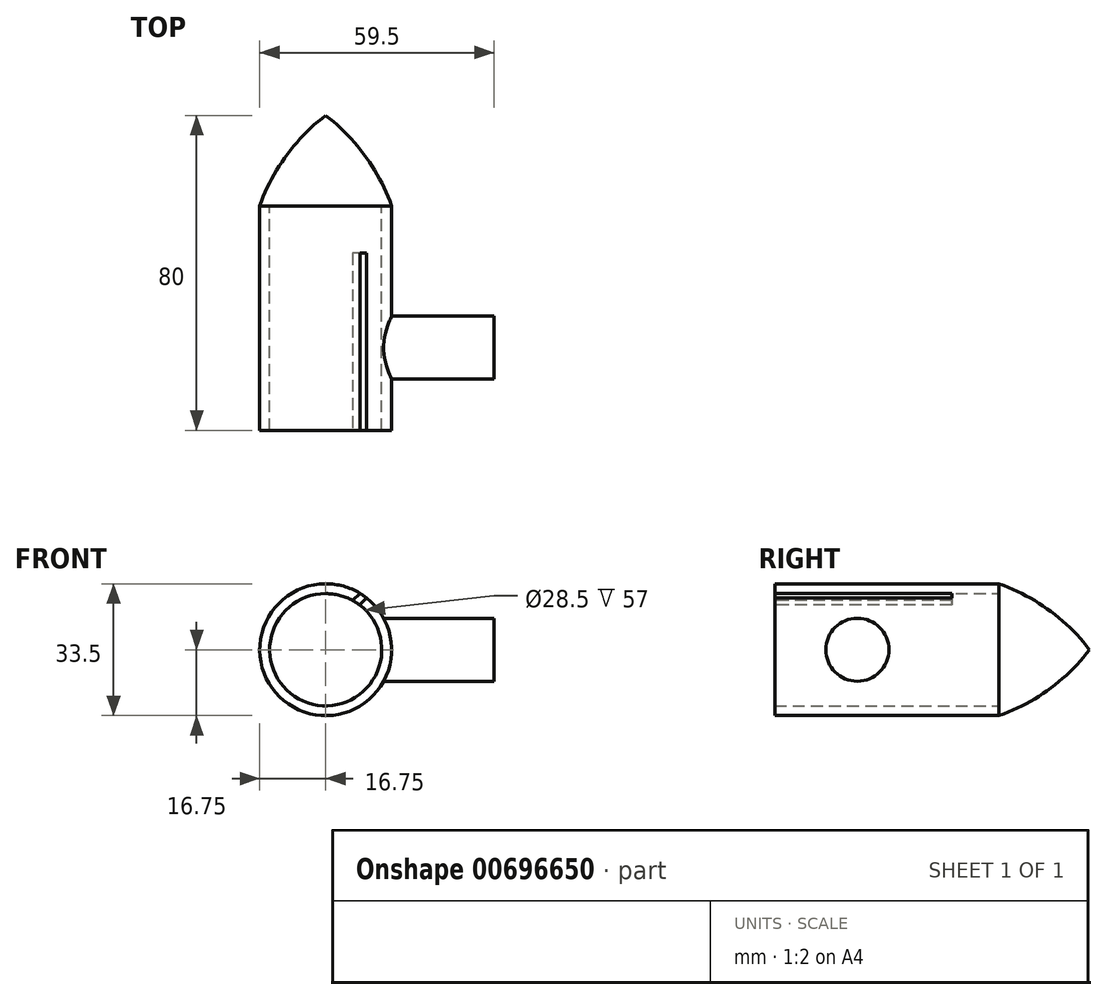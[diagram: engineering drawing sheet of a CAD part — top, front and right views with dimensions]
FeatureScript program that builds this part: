
annotation { "Feature Type Name" : "Feature", "Feature Type Description" : "" }
export const myFeature = defineFeature(function(context is Context, id is Id, definition is map)
    precondition{}
    {
        {
            var Q0;
            Q0=qCreatedBy(makeId("Top.planeOp"),FACE);
            var sketch = newSketch(context, id + "F0", { "sketchPlane" : qUnion([Q0])});
            skLineSegment(sketch, "E0.top", {"start": v(14.25, -19) * mm, "end": v(16.75, -19) * mm});
            skLineSegment(sketch, "E0.left", {"start": v(0, 61) * mm, "end": v(0, 38) * mm});
            skLineSegment(sketch, "E0.right", {"start": v(16.75, 38) * mm, "end": v(16.75, -19) * mm});
            skLineSegment(sketch, "E1", {"start": v(8.38, 61) * mm, "end": v(8.38, 38) * mm, "construction": true});
            skArc(sketch, "E2", {"start": v(16.75, 38) * mm, "mid": v(10.05, 50.7) * mm, "end": v(0, 61) * mm});
            skLineSegment(sketch, "E3.right", {"start": v(14.25, -19) * mm, "end": v(14.25, 38) * mm});
            skLineSegment(sketch, "E4", {"start": v(0, 38) * mm, "end": v(14.25, 38) * mm});
            skPoint(sketch, "E5.orphan", {"position": v(16.75, 61) * mm});
            skPoint(sketch, "E6", {"position": v(16.75, 17.48) * mm});
            skSolve(sketch);
        }
        {
            var Q0;
            Q0 = qSketchRegion(id + "F0", true);
            var Q1;
            Q1=sQuery(id+"F0.wireOp",EDGE,"E0.left");
            revolve(context, id + "F1", {"entities" : qUnion([Q0]), "axis" : qUnion([Q1]), "revolveType" : RevolveType.FULL});
        }
        {
            var Q0;
            Q0=sQuery(id+"F0.wireOp",VERTEX,"E6");
            var Q1;
            Q1=qCreatedBy(makeId("Right.planeOp"),FACE);
            cPlane(context, id + "F2", {"entities" : qUnion([Q0, Q1]), "cplaneType" : CPlaneType.PLANE_POINT, "offset" : 25 * mm, "width" : 150 * mm, "height" : 150 * mm});
        }
        {
            var Q0;
            Q0=qCreatedBy(id+"F2.planeOp",FACE);
            var sketch = newSketch(context, id + "F3", { "sketchPlane" : qUnion([Q0])});
            skLineSegment(sketch, "E7.0", {"start": v(-19, 16.75) * mm, "end": v(-19, -16.75) * mm});
            skLineSegment(sketch, "E8", {"start": v(-19, 16.75) * mm, "end": v(38, 16.75) * mm});
            skLineSegment(sketch, "E9", {"start": v(38, -16.75) * mm, "end": v(-19, -16.75) * mm});
            skPoint(sketch, "E10.start.orphan", {"position": v(-19, 0) * mm});
            skCircle(sketch, "E11", {"center": v(2, 0) * mm, "radius": 8 * mm});
            skSolve(sketch);
        }
        {
            var Q0;
            Q0 = qSketchRegion(id + "F3", true);
            var Q1;
            Q1=makeQuery(id+"F1.opRevolve","SWEPT_FACE",FACE,{"disambiguationData":[OSD([sQuery(id+"F0.wireOp",EDGE,"E0.right")])]});
            extrude(context, id + "F4", {"entities" : qUnion([Q0]), "operationType" : NewBodyOperationType.ADD, "depth" : 26 * mm, "offsetDistance" : 25 * mm, "hasSecondDirection" : true, "secondDirectionBound" : SecondDirectionBoundingType.UP_TO_SURFACE, "secondDirectionOppositeDirection" : true, "secondDirectionDepth" : 25 * mm, "secondDirectionBoundEntityFace" : qUnion([Q1])});
        }
        {
            var Q0;
            Q0=makeQuery(id+"F1.opRevolve","SWEPT_FACE",FACE,{"disambiguationData":[OSD([sQuery(id+"F0.wireOp",EDGE,"E0.top")])]});
            cPlane(context, id + "F5", {"entities" : qUnion([Q0]), "cplaneType" : CPlaneType.OFFSET, "offset" : 0 * mm, "width" : 150 * mm, "height" : 150 * mm});
        }
        {
            var Q0;
            Q0=qCreatedBy(id+"F5.planeOp",FACE);
            var sketch = newSketch(context, id + "F6", { "sketchPlane" : qUnion([Q0])});
            skArc(sketch, "E12.0", {"start": v(10.35, 13.17) * mm, "mid": v(9.53, 13.78) * mm, "end": v(8.67, 14.33) * mm});
            skLineSegment(sketch, "E13.0", {"start": v(10.35, 13.17) * mm, "end": v(8.56, 11.4) * mm});
            skLineSegment(sketch, "E14.0", {"start": v(8.67, 14.33) * mm, "end": v(6.84, 12.5) * mm});
            skArc(sketch, "E15.0", {"start": v(8.56, 11.4) * mm, "mid": v(7.72, 11.98) * mm, "end": v(6.84, 12.5) * mm});
            skSolve(sketch);
        }
        {
            var Q0;
            Q0 = qSketchRegion(id + "F6", true);
            extrude(context, id + "F7", {"entities" : qUnion([Q0]), "operationType" : NewBodyOperationType.REMOVE, "oppositeDirection" : true, "depth" : 45 * mm, "offsetDistance" : 25 * mm});
        }
    });
